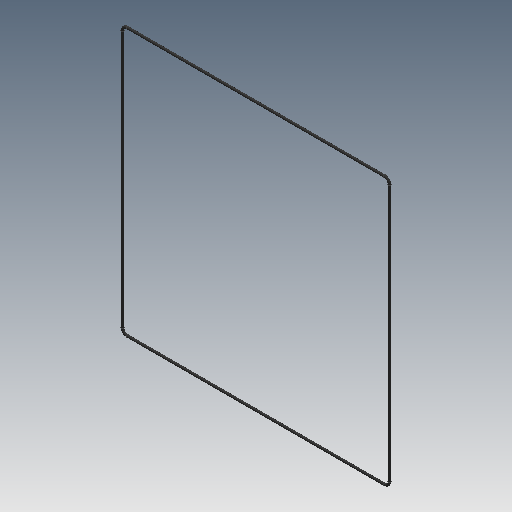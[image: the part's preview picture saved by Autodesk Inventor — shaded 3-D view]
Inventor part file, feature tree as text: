
AUTODESK INVENTOR PART (.ipt)
format: ipt  version: 2018.2 (Build 222227000, 227)  size: 124,416 bytes
history: native  units: mm
features: fillet x3, extrude x1, sketch x1
ambient origin geometry x8: Origin, YZ Plane, XZ Plane, XY Plane, X Axis, Y Axis, Z Axis, Center Point
bodies: Solid1 (feature_tree)
feature tree (5):
  extrude  "Extrusion1"  Depth=1.5875mm
  fillet  "Fillet1"  Radius=20.0mm
  fillet  "Fillet3"  Radius=4.7625mm
  fillet  "Fillet2"  Radius=3.175mm
  sketch  "Sketch1"  dims[d0=300.0mm d1=300.0mm d2=20.0mm d3=4.7625mm d4=3.175mm d5=3.175mm d6=0.0mm d7=7.9375mm d8=1.5875mm d9=4.7625mm]
